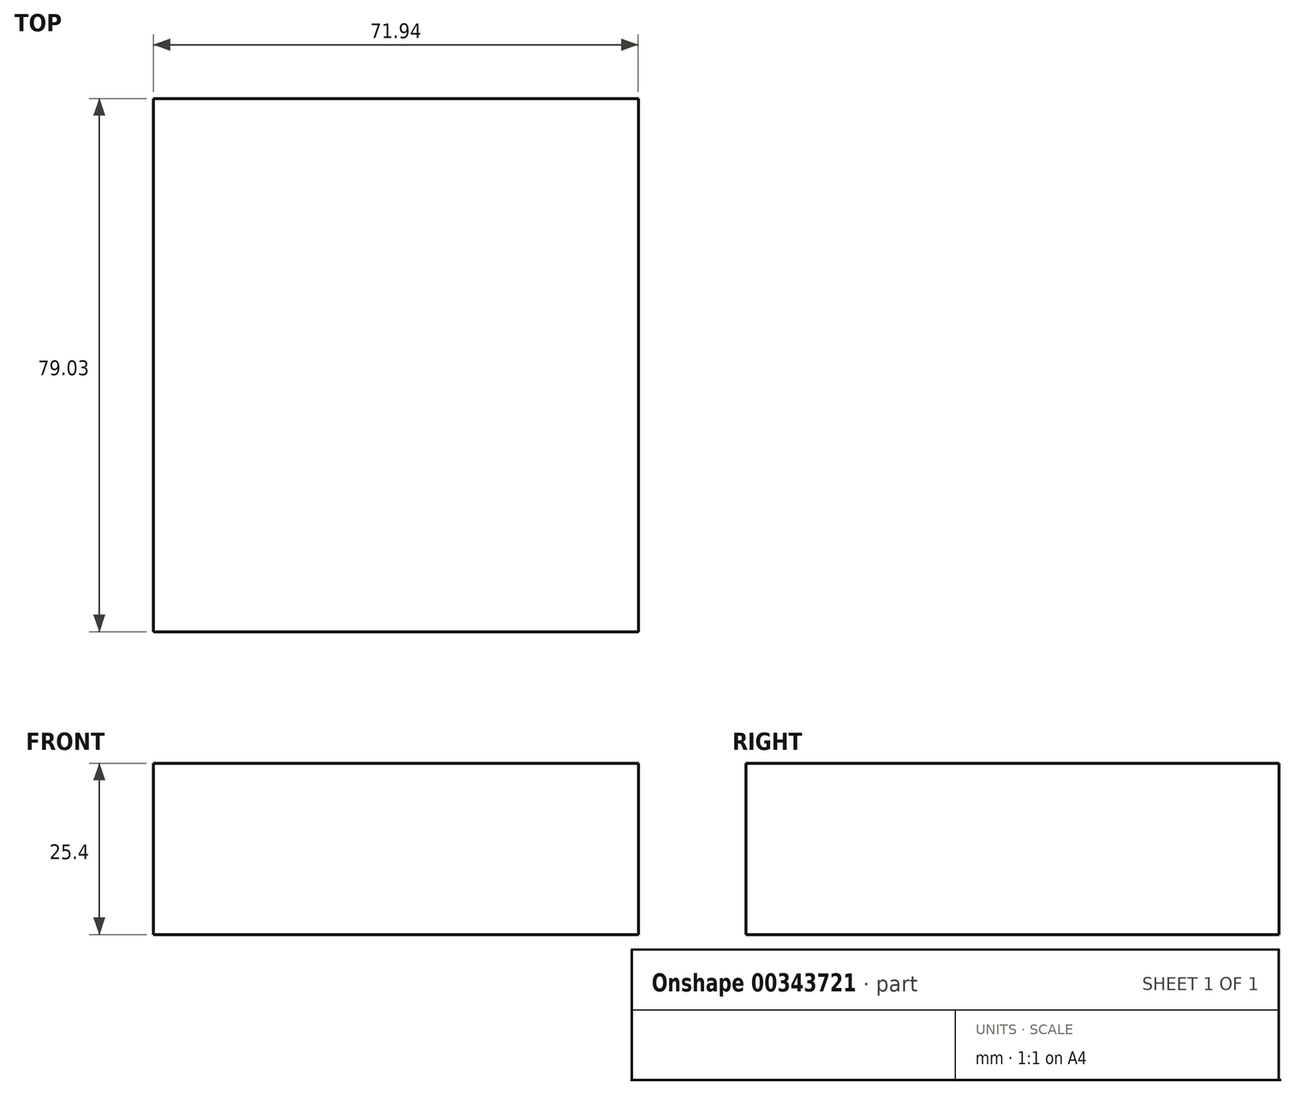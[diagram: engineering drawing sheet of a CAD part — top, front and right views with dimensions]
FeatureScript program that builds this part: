
annotation { "Feature Type Name" : "Feature", "Feature Type Description" : "" }
export const myFeature = defineFeature(function(context is Context, id is Id, definition is map)
    precondition{}
    {
        {
            var Q0;
            Q0=qCreatedBy(makeId("Top.planeOp"),FACE);
            var sketch = newSketch(context, id + "F0", { "sketchPlane" : qUnion([Q0])});
            skLineSegment(sketch, "E0.bottom", {"start": v(-33.09, 42.43) * mm, "end": v(38.85, 42.43) * mm});
            skLineSegment(sketch, "E0.top", {"start": v(-33.09, -36.6) * mm, "end": v(38.85, -36.6) * mm});
            skLineSegment(sketch, "E0.left", {"start": v(-33.09, 42.43) * mm, "end": v(-33.09, -36.6) * mm});
            skLineSegment(sketch, "E0.right", {"start": v(38.85, 42.43) * mm, "end": v(38.85, -36.6) * mm});
            skSolve(sketch);
        }
        {
            var Q0;
            Q0 = qSketchRegion(id + "F0", true);
            extrude(context, id + "F1", {"entities" : qUnion([Q0]), "depth" : 25.4 * mm});
        }
    });
